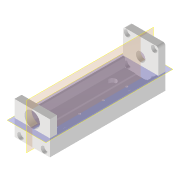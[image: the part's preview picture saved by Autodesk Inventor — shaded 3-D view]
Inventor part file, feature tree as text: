
AUTODESK INVENTOR PART (.ipt)
format: ipt  version: 2022 (Build 260153000, 153)  size: 189,952 bytes
history: native  units: mm
features: other x2, plane x2
ambient origin geometry x8: Origin, YZ Plane, XZ Plane, XY Plane, X Axis, Y Axis, Z Axis, Center Point
bodies: Volumenkörper2 (feature_tree), Volumenkörper3 (feature_tree), Volumenkörper4 (feature_tree), Volumenkörper1 (feature_tree)
feature tree (4):
  other  "Volumenkörper3:1"
  plane  "Arbeitsebene1"
  plane  "Arbeitsebene2"
  other  "Volumenkörper2:1"
